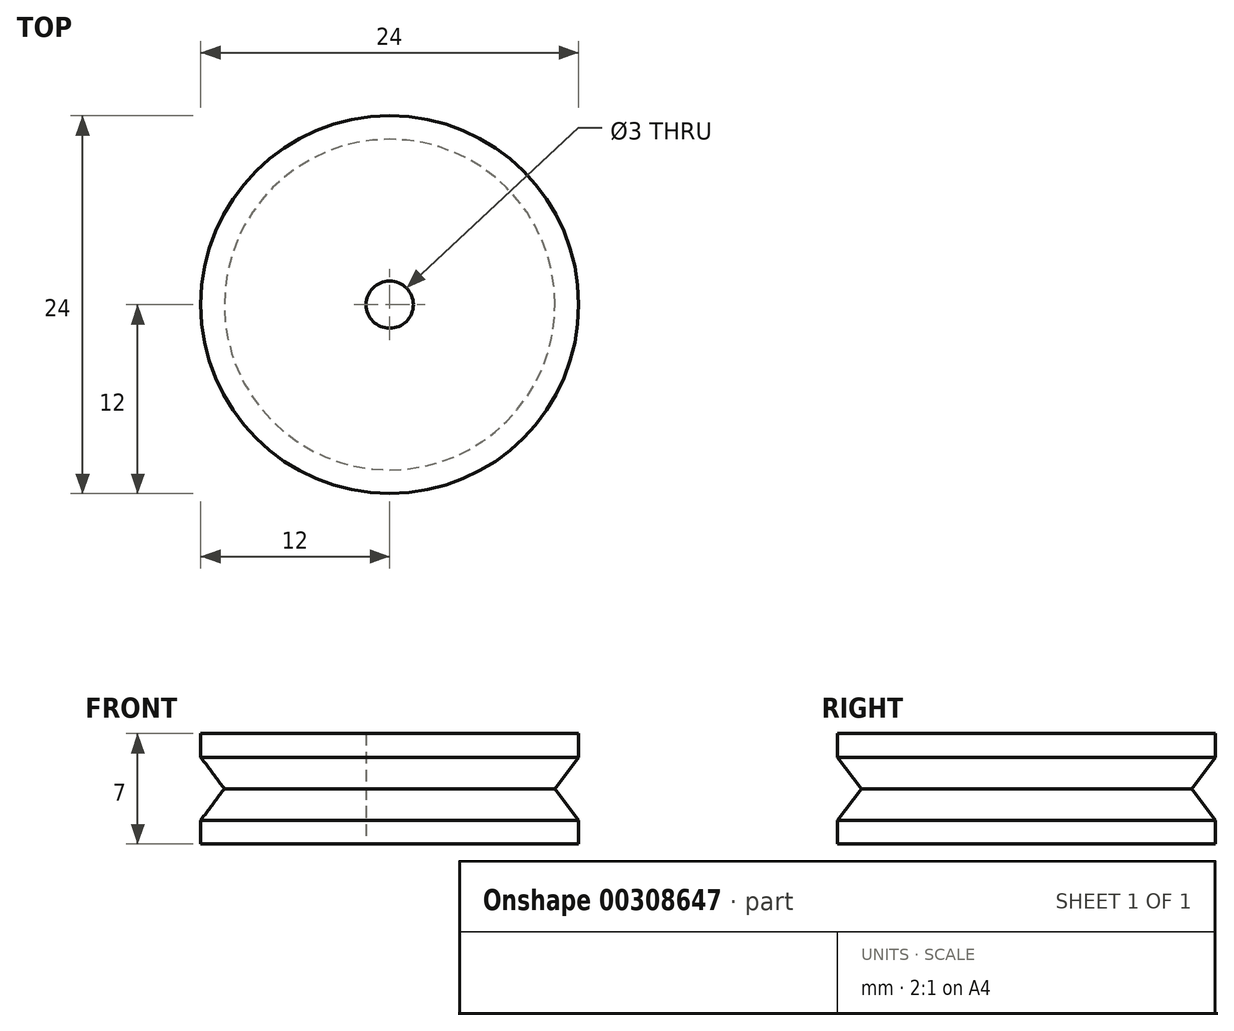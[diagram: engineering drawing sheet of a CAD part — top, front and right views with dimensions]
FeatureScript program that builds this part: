
annotation { "Feature Type Name" : "Feature", "Feature Type Description" : "" }
export const myFeature = defineFeature(function(context is Context, id is Id, definition is map)
    precondition{}
    {
        {
            var Q0;
            Q0=qCreatedBy(makeId("Front.planeOp"),FACE);
            var sketch = newSketch(context, id + "F0", { "sketchPlane" : qUnion([Q0])});
            skLineSegment(sketch, "E0", {"start": v(-1.5, 0) * mm, "end": v(-1.5, 3.5) * mm});
            skLineSegment(sketch, "E1", {"start": v(-1.5, 3.5) * mm, "end": v(-12, 3.5) * mm});
            skLineSegment(sketch, "E2", {"start": v(-12, 3.5) * mm, "end": v(-12, 2) * mm});
            skLineSegment(sketch, "E3", {"start": v(-12, 2) * mm, "end": v(-10.5, 0) * mm});
            skLineSegment(sketch, "E4", {"start": v(-10.5, 0) * mm, "end": v(-1.5, 0) * mm});
            skLineSegment(sketch, "E5.MirrorCS", {"start": v(-12, -2) * mm, "end": v(-10.5, 0) * mm});
            skLineSegment(sketch, "E6.MirrorCS", {"start": v(-12, -3.5) * mm, "end": v(-12, -2) * mm});
            skLineSegment(sketch, "E7.MirrorCS", {"start": v(-1.5, -3.5) * mm, "end": v(-12, -3.5) * mm});
            skLineSegment(sketch, "E8.MirrorCS", {"start": v(-1.5, 0) * mm, "end": v(-1.5, -3.5) * mm});
            skLineSegment(sketch, "E9", {"start": v(0, 0) * mm, "end": v(0, 2) * mm});
            skSolve(sketch);
        }
        {
            var Q0;
            Q0=makeQuery(id+"F0.imprint","IMPRINT",FACE,{"disambiguationData":[TD([[makeQuery(id+"F0.imprint","IMPRINT",EDGE,{"derivedFrom":sQuery(id+"F0.wireOp",EDGE,"E0")}),1.0]])]});
            var Q1;
            Q1=makeQuery(id+"F0.imprint","IMPRINT",FACE,{"disambiguationData":[TD([[makeQuery(id+"F0.imprint","IMPRINT",EDGE,{"derivedFrom":sQuery(id+"F0.wireOp",EDGE,"E4")}),-1.0]])]});
            var Q2;
            Q2=sQuery(id+"F0.wireOp",EDGE,"E9");
            revolve(context, id + "F1", {"entities" : qUnion([Q0, Q1]), "axis" : qUnion([Q2]), "revolveType" : RevolveType.FULL});
        }
    });
